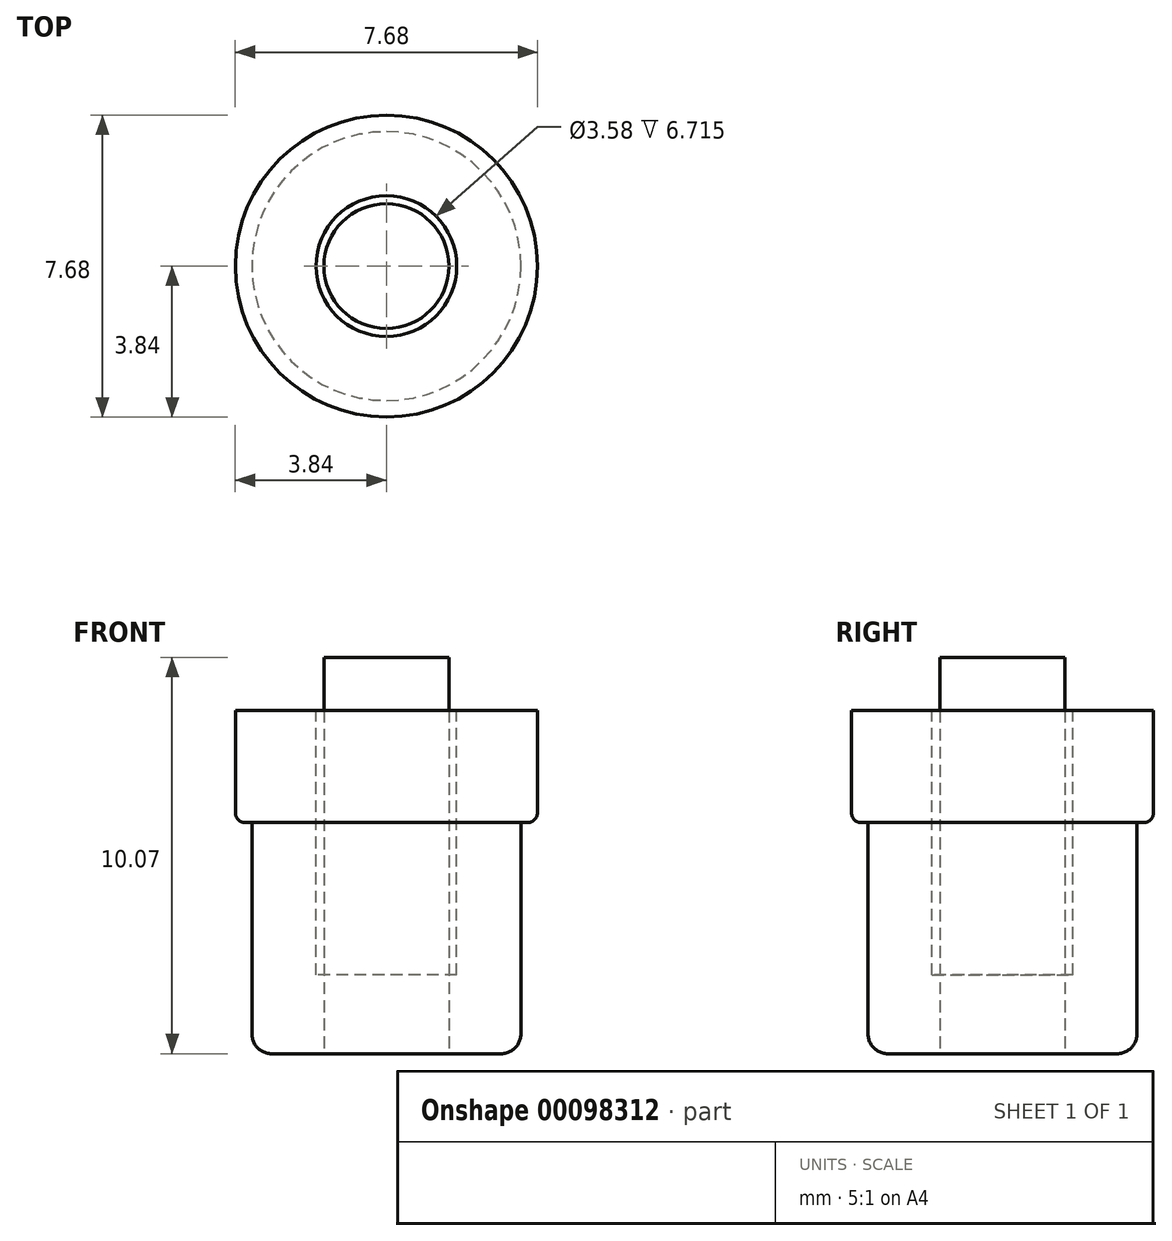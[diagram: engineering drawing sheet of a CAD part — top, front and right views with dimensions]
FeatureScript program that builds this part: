
annotation { "Feature Type Name" : "Feature", "Feature Type Description" : "" }
export const myFeature = defineFeature(function(context is Context, id is Id, definition is map)
    precondition{}
    {
        {
            var Q0;
            Q0=qCreatedBy(makeId("Front.planeOp"),FACE);
            var sketch = newSketch(context, id + "F0", { "sketchPlane" : qUnion([Q0])});
            skLineSegment(sketch, "E0", {"start": v(0, 0) * mm, "end": v(-3.42, 0) * mm});
            skLineSegment(sketch, "E1", {"start": v(-3.42, 0) * mm, "end": v(-3.42, 5.87) * mm});
            skLineSegment(sketch, "E2", {"start": v(-3.42, 5.87) * mm, "end": v(-3.84, 5.87) * mm});
            skLineSegment(sketch, "E3", {"start": v(-3.84, 5.87) * mm, "end": v(-3.84, 8.72) * mm});
            skLineSegment(sketch, "E4", {"start": v(-3.84, 8.72) * mm, "end": v(-1.79, 8.72) * mm});
            skLineSegment(sketch, "E5", {"start": v(-1.79, 8.72) * mm, "end": v(-1.79, 2) * mm});
            skLineSegment(sketch, "E6", {"start": v(-1.79, 2) * mm, "end": v(0, 2) * mm});
            skLineSegment(sketch, "E7", {"start": v(0, 2) * mm, "end": v(0, 0) * mm});
            skSolve(sketch);
        }
        {
            var Q0;
            Q0 = qSketchRegion(id + "F0", true);
            var Q1;
            Q1=sQuery(id+"F0.wireOp",EDGE,"E7");
            revolve(context, id + "F1", {"entities" : qUnion([Q0]), "axis" : qUnion([Q1]), "revolveType" : RevolveType.FULL});
        }
        {
            var Q0;
            Q0=makeQuery(id+"F1.opRevolve","SWEPT_EDGE",EDGE,{"disambiguationData":[OSD([sQuery(id+"F0.wireOp",EDGE,"E2"),sQuery(id+"F0.wireOp",EDGE,"E3")])]});
            fillet(context, id + "F2", {"entities" : qUnion([Q0]), "radius" : 0.25 * mm, "allowEdgeOverflow" : false});
        }
        {
            var Q0;
            Q0=makeQuery(id+"F1.opRevolve","SWEPT_EDGE",EDGE,{"disambiguationData":[OSD([sQuery(id+"F0.wireOp",EDGE,"E0"),sQuery(id+"F0.wireOp",EDGE,"E1")])]});
            fillet(context, id + "F3", {"entities" : qUnion([Q0]), "radius" : 0.5 * mm, "allowEdgeOverflow" : false});
        }
        {
            var Q0;
            Q0=qCreatedBy(makeId("Front.planeOp"),FACE);
            var sketch = newSketch(context, id + "F4", { "sketchPlane" : qUnion([Q0])});
            skLineSegment(sketch, "E8.bottom", {"start": v(0, 0) * mm, "end": v(-1.59, 0) * mm});
            skLineSegment(sketch, "E8.top", {"start": v(0, 10.07) * mm, "end": v(-1.59, 10.07) * mm});
            skLineSegment(sketch, "E8.left", {"start": v(0, 0) * mm, "end": v(0, 10.07) * mm});
            skLineSegment(sketch, "E8.right", {"start": v(-1.59, 0) * mm, "end": v(-1.59, 10.07) * mm});
            skSolve(sketch);
        }
        {
            var Q0;
            Q0 = qSketchRegion(id + "F4", true);
            var Q1;
            Q1=sQuery(id+"F4.wireOp",EDGE,"E8.left");
            revolve(context, id + "F5", {"entities" : qUnion([Q0]), "axis" : qUnion([Q1]), "revolveType" : RevolveType.FULL});
        }
    });
